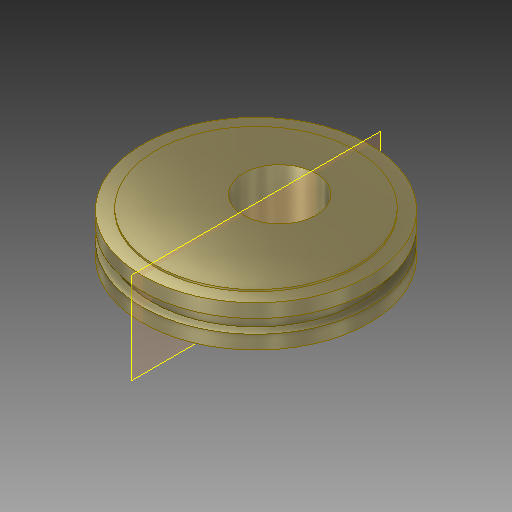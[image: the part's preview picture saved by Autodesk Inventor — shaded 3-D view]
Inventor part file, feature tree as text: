
AUTODESK INVENTOR PART (.ipt)
format: ipt  version: 2017 (Build 210142000, 142)  size: 190,464 bytes
history: native  units: mm
features: extrude x7, sketch x6, projected_geometry x2, plane x1
ambient origin geometry x8: Origin, YZ Plane, XZ Plane, XY Plane, X Axis, Y Axis, Z Axis, Center Point
bodies: Solid1 (feature_tree)
feature tree (16):
  extrude  "Extrusion1"  Depth=1.5mm TaperAngle=0.0deg
  extrude  "Extrusion2"  Depth=1.5mm TaperAngle=0.0deg
  extrude  "Extrusion3"  Depth=1.5mm TaperAngle=0.0deg
  sketch  "Sketch4"  dims[d9=3.0mm d17=13.5mm]
  extrude  "Extrusion6"  Depth=3.0mm
  extrude  "Extrusion7"  Depth=4.45mm TaperAngle=0.0deg
  plane  "Work Plane1"
  extrude  "Extrusion8"  Depth=10.0mm
  extrude  "Extrusion10"  Depth=10.0mm
  sketch  "Sketch1"  dims[d0=23.0mm d1=1.5mm d2=0.0mm]
  sketch  "Sketch2"  dims[d3=25.0mm d4=1.5mm d5=0.0mm]
  sketch  "Sketch3"  dims[d6=25.0mm d7=1.5mm d8=0.0mm]
  projected_geometry  "Projected Loop1"
  sketch  "Sketch6"  dims[d18=8.0mm d19=4.45mm d20=0.0mm]
  projected_geometry  "Projected Loop2"
  sketch  "Sketch7"  dims[d21=10.0mm d22=0.0mm d23=6.76mm d24=4.45mm d25=13.5mm d26=6.75mm d27=2.225mm d28=10.0mm d29=1.6mm d30=4.45mm d31=0.0mm d32=22.0mm d35=0.2mm d36=0.0mm]
